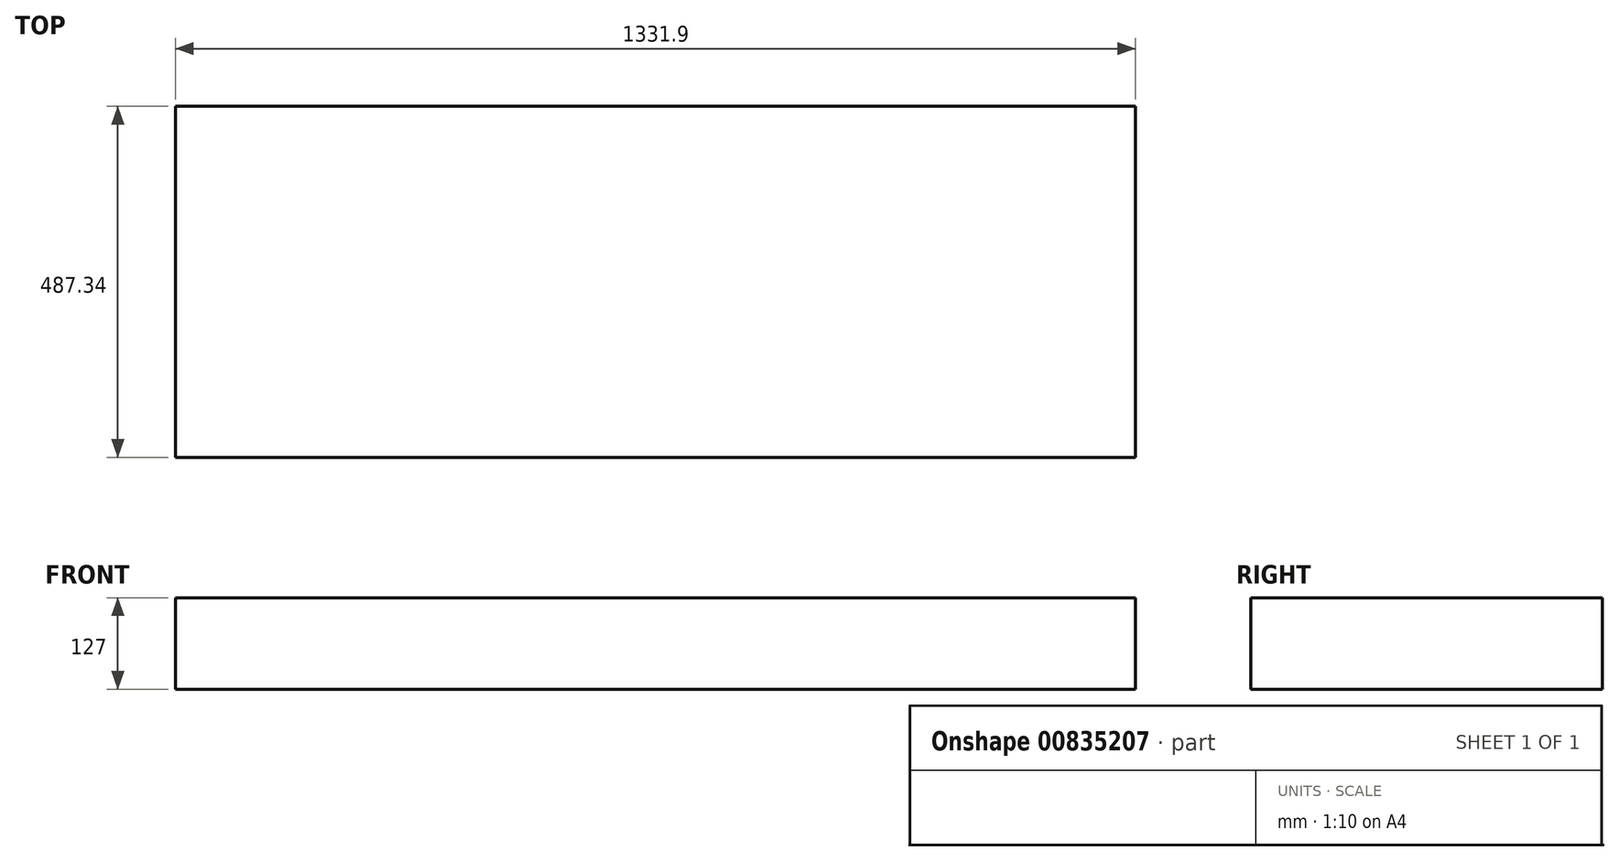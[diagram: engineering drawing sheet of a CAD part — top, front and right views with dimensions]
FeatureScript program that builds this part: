
annotation { "Feature Type Name" : "Feature", "Feature Type Description" : "" }
export const myFeature = defineFeature(function(context is Context, id is Id, definition is map)
    precondition{}
    {
        {
            var Q0;
            Q0=qCreatedBy(makeId("Top.planeOp"),FACE);
            var sketch = newSketch(context, id + "F0", { "sketchPlane" : qUnion([Q0])});
            skLineSegment(sketch, "E0.bottom", {"start": v(-665.95, 243.67) * mm, "end": v(665.95, 243.67) * mm});
            skLineSegment(sketch, "E0.top", {"start": v(-665.95, -243.67) * mm, "end": v(665.95, -243.67) * mm});
            skLineSegment(sketch, "E0.left", {"start": v(-665.95, 243.67) * mm, "end": v(-665.95, -243.67) * mm});
            skLineSegment(sketch, "E0.right", {"start": v(665.95, 243.67) * mm, "end": v(665.95, -243.67) * mm});
            skPoint(sketch, "E0.middle", {"position": v(0, 0) * mm});
            skSolve(sketch);
        }
        {
            var Q0;
            Q0 = qSketchRegion(id + "F0", true);
            extrude(context, id + "F1", {"entities" : qUnion([Q0]), "endBound" : BoundingType.SYMMETRIC, "depth" : 127 * mm, "offsetDistance" : 25.4 * mm});
        }
    });
